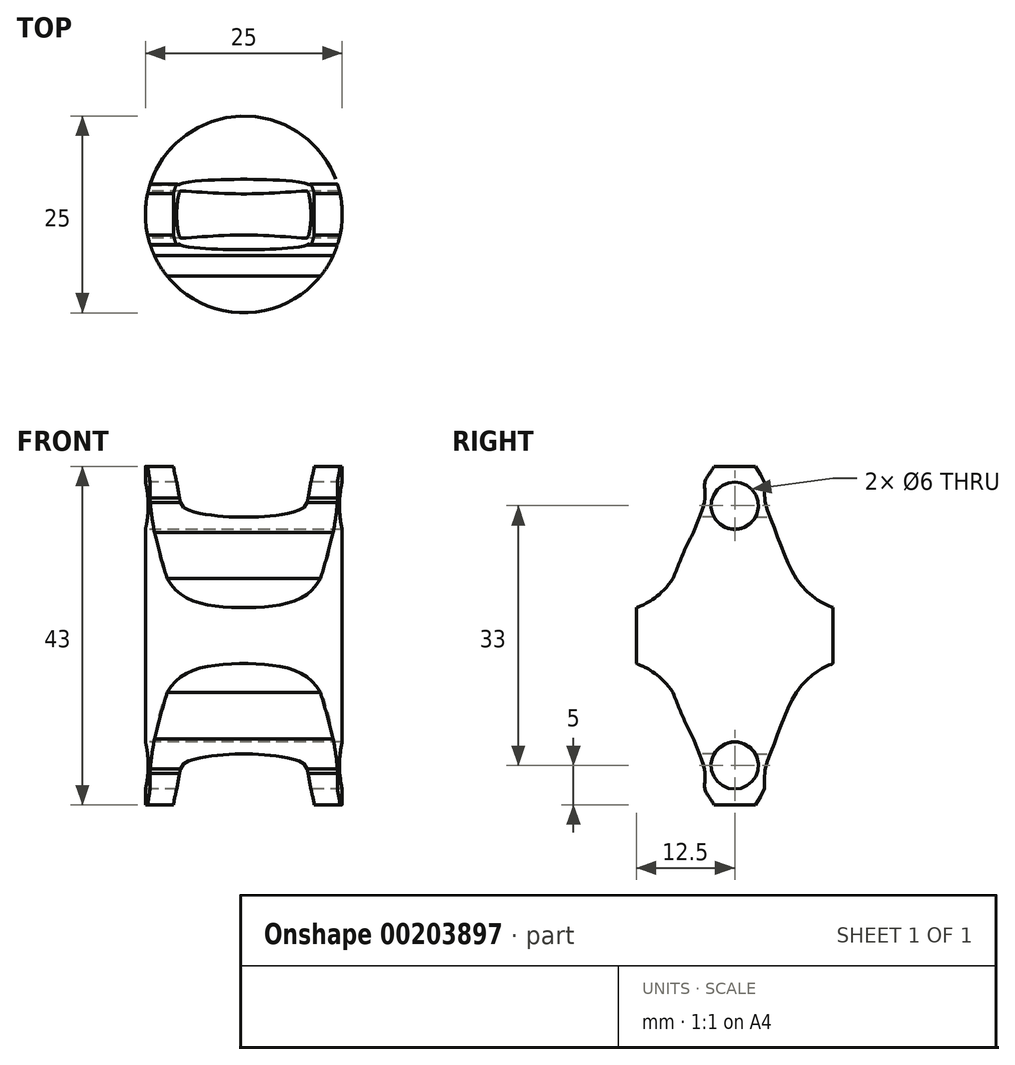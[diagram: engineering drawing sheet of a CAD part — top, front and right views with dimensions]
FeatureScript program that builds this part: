
annotation { "Feature Type Name" : "Feature", "Feature Type Description" : "" }
export const myFeature = defineFeature(function(context is Context, id is Id, definition is map)
    precondition{}
    {
        {
            var Q0;
            Q0=qCreatedBy(makeId("Top.planeOp"),FACE);
            var sketch = newSketch(context, id + "F0", { "sketchPlane" : qUnion([Q0])});
            skCircle(sketch, "E0", {"center": v(0, 0) * mm, "radius": 12.5 * mm});
            skSolve(sketch);
        }
        {
            var Q0;
            Q0=makeQuery(id+"F0.imprint","IMPRINT",FACE,{"disambiguationData":[TD([[makeQuery(id+"F0.imprint","IMPRINT",EDGE,{"derivedFrom":sQuery(id+"F0.wireOp",EDGE,"E0")}),1.0]])]});
            extrude(context, id + "F1", {"entities" : qUnion([Q0]), "depth" : 3.5 * mm});
        }
        {
            var Q0;
            Q0=makeQuery(id+"F1.opExtrude","CAP_FACE",FACE,{"disambiguationData":[OSD([sQuery(id+"F0.wireOp",EDGE,"E0")])],"isStart":false});
            extrude(context, id + "F2", {"entities" : qUnion([Q0]), "operationType" : NewBodyOperationType.ADD, "depth" : 18 * mm});
        }
        {
            var Q0;
            Q0=qCreatedBy(makeId("Right.planeOp"),FACE);
            var sketch = newSketch(context, id + "F3", { "sketchPlane" : qUnion([Q0])});
            skCircle(sketch, "E1", {"center": v(0, 16.5) * mm, "radius": 3 * mm});
            skLineSegment(sketch, "E2", {"start": v(-12.63, 3.5) * mm, "end": v(12.63, 3.5) * mm});
            skFitSpline(sketch, "E3", {"points": [v(-12.63, 3.5) * mm, v(-7.83, 7.25) * mm, v(-5.24, 13.1) * mm, v(-3.77, 17.5) * mm, v(-3.77, 19.53) * mm, v(-2.65, 21.5) * mm], "startDerivative": vector(24.86, 8.48) * mm, "endDerivative": vector(7.63, 15.3) * mm});
            skFitSpline(sketch, "E4", {"points": [v(-3.77, 17.5) * mm, v(-5.24, 13.1) * mm, v(-7.83, 7.25) * mm], "startDerivative": vector(-3.74, -25.65) * mm, "endDerivative": vector(-2.37, -6.27) * mm});
            skFitSpline(sketch, "E5.MirrorCS", {"points": [v(12.63, 3.5) * mm, v(7.83, 7.25) * mm, v(5.24, 13.1) * mm, v(3.77, 17.5) * mm, v(3.77, 19.53) * mm, v(2.65, 21.5) * mm], "startDerivative": vector(-24.86, 8.48) * mm, "endDerivative": vector(-7.63, 15.3) * mm});
            skLineSegment(sketch, "E6", {"start": v(-1.86, 21.5) * mm, "end": v(2.65, 21.5) * mm});
            skLineSegment(sketch, "E7", {"start": v(-12.5, 0) * mm, "end": v(-12.5, 31) * mm});
            skLineSegment(sketch, "E8", {"start": v(12.5, 31) * mm, "end": v(12.5, 0) * mm});
            skLineSegment(sketch, "E9", {"start": v(-12.5, 0) * mm, "end": v(12.5, 0) * mm});
            skLineSegment(sketch, "E10", {"start": v(-2.65, 21.5) * mm, "end": v(2.65, 21.5) * mm});
            skSolve(sketch);
        }
        {
            var Q0;
            Q0=qSketchRegion(id+"F3",true);
            extrude(context, id + "F4", {"entities" : qUnion([Q0]), "operationType" : NewBodyOperationType.INTERSECT, "depth" : 25 * mm, "hasSecondDirection" : true, "secondDirectionOppositeDirection" : true, "secondDirectionDepth" : 25 * mm});
        }
        {
            var Q0;
            Q0=qCreatedBy(makeId("Front.planeOp"),FACE);
            var sketch = newSketch(context, id + "F5", { "sketchPlane" : qUnion([Q0])});
            skFitSpline(sketch, "E11.0", {"points": [v(-11.71, 31) * mm, v(-11.62, 30.5) * mm, v(-11.48, 29.74) * mm, v(-11.34, 28.68) * mm, v(-11.27, 27.86) * mm, v(-11.23, 27.02) * mm, v(-11.2, 25.9) * mm, v(-11.16, 24.47) * mm, v(-11.1, 23.06) * mm, v(-11.02, 21.95) * mm, v(-10.91, 21.12) * mm, v(-10.76, 20.31) * mm, v(-10.59, 19.5) * mm, v(-10.43, 18.84) * mm, v(-10.32, 18.3) * mm, v(-10.23, 17.74) * mm, v(-10.12, 17.03) * mm, v(-9.97, 16.35) * mm, v(-9.8, 15.85) * mm, v(-9.62, 15.5) * mm, v(-9.42, 15.2) * mm, v(-9.1, 14.86) * mm, v(-8.66, 14.52) * mm, v(-8.06, 14.2) * mm, v(-7.4, 13.96) * mm, v(-6.72, 13.76) * mm, v(-6, 13.59) * mm, v(-5.23, 13.44) * mm, v(-4.44, 13.32) * mm, v(-3.63, 13.23) * mm, v(-2.8, 13.15) * mm, v(-1.95, 13.1) * mm, v(-1.1, 13.06) * mm, v(0.05, 13.04) * mm, v(1.19, 13.06) * mm, v(2.33, 13.12) * mm, v(3.45, 13.2) * mm, v(4.53, 13.33) * mm, v(5.56, 13.5) * mm, v(6.32, 13.66) * mm, v(7.03, 13.84) * mm, v(7.7, 14.06) * mm, v(8.33, 14.34) * mm, v(8.81, 14.63) * mm, v(9.16, 14.92) * mm, v(9.4, 15.17) * mm, v(9.6, 15.46) * mm, v(9.77, 15.8) * mm, v(9.9, 16.18) * mm, v(10.05, 16.7) * mm, v(10.18, 17.4) * mm, v(10.3, 18.24) * mm, v(10.48, 19.06) * mm, v(10.67, 19.86) * mm, v(10.83, 20.67) * mm, v(10.97, 21.5) * mm, v(11.06, 22.35) * mm, v(11.1, 23.23) * mm, v(11.15, 24.4) * mm, v(11.19, 25.88) * mm, v(11.24, 27.35) * mm, v(11.32, 28.5) * mm, v(11.46, 29.64) * mm, v(11.61, 30.46) * mm, v(11.71, 31) * mm]});
            skFitSpline(sketch, "E12.0", {"points": [v(-9.75, 31.36) * mm, v(-9.7, 31.11) * mm, v(-9.6, 30.6) * mm, v(-9.47, 29.78) * mm, v(-9.35, 28.9) * mm, v(-9.28, 28) * mm, v(-9.23, 27.1) * mm, v(-9.2, 25.95) * mm, v(-9.16, 24.8) * mm, v(-9.13, 23.7) * mm, v(-9.1, 23.04) * mm, v(-9.06, 22.52) * mm, v(-9.03, 22.15) * mm, v(-8.98, 21.8) * mm, v(-8.91, 21.31) * mm, v(-8.8, 20.72) * mm, v(-8.67, 20.09) * mm, v(-8.54, 19.55) * mm, v(-8.46, 19.19) * mm, v(-8.4, 18.88) * mm, v(-8.36, 18.65) * mm, v(-8.32, 18.42) * mm, v(-8.27, 18.13) * mm, v(-8.21, 17.78) * mm, v(-8.12, 17.27) * mm, v(-8.03, 16.87) * mm, v(-7.94, 16.6) * mm, v(-7.88, 16.49) * mm, v(-7.85, 16.45) * mm, v(-7.82, 16.42) * mm, v(-7.78, 16.37) * mm, v(-7.71, 16.31) * mm, v(-7.6, 16.23) * mm, v(-7.43, 16.14) * mm, v(-7.17, 16.01) * mm, v(-6.78, 15.86) * mm, v(-6.21, 15.7) * mm, v(-5.59, 15.54) * mm, v(-4.9, 15.42) * mm, v(-4.17, 15.3) * mm, v(-3.42, 15.22) * mm, v(-2.65, 15.15) * mm, v(-1.85, 15.1) * mm, v(-1.03, 15.06) * mm, v(0.05, 15.04) * mm, v(1.12, 15.06) * mm, v(2.2, 15.11) * mm, v(3.26, 15.2) * mm, v(4.26, 15.31) * mm, v(5.2, 15.47) * mm, v(5.87, 15.6) * mm, v(6.47, 15.76) * mm, v(7, 15.94) * mm, v(7.36, 16.1) * mm, v(7.57, 16.22) * mm, v(7.7, 16.3) * mm, v(7.79, 16.38) * mm, v(7.84, 16.44) * mm, v(7.87, 16.48) * mm, v(7.93, 16.6) * mm, v(8, 16.77) * mm, v(8.07, 17.04) * mm, v(8.14, 17.36) * mm, v(8.2, 17.73) * mm, v(8.26, 18.07) * mm, v(8.3, 18.37) * mm, v(8.35, 18.6) * mm, v(8.4, 18.83) * mm, v(8.45, 19.13) * mm, v(8.53, 19.5) * mm, v(8.62, 19.9) * mm, v(8.71, 20.3) * mm, v(8.8, 20.67) * mm, v(8.89, 21.16) * mm, v(8.98, 21.75) * mm, v(9.09, 22.76) * mm, v(9.15, 24.16) * mm, v(9.18, 25.63) * mm, v(9.22, 26.83) * mm, v(9.26, 27.6) * mm, v(9.3, 28.22) * mm, v(9.35, 28.85) * mm, v(9.45, 29.64) * mm, v(9.6, 30.54) * mm, v(9.7, 31.1) * mm, v(9.75, 31.36) * mm]});
            skLineSegment(sketch, "E13", {"start": v(12.22, 21.5) * mm, "end": v(10.23, 21.71) * mm});
            skLineSegment(sketch, "E14", {"start": v(-12.22, 21.5) * mm, "end": v(-10.23, 21.71) * mm});
            skLineSegment(sketch, "E15", {"start": v(10.23, 21.71) * mm, "end": v(-10.23, 21.71) * mm});
            skSolve(sketch);
        }
        {
            var Q0;
            Q0=makeQuery(id+"F5.imprint","IMPRINT",FACE,{"disambiguationData":[TD([[makeQuery(id+"F5.imprint","IMPRINT",EDGE,{"derivedFrom":sQuery(id+"F5.wireOp",EDGE,"E12.0")}),1.0]])]});
            extrude(context, id + "F6", {"entities" : qUnion([Q0]), "operationType" : NewBodyOperationType.REMOVE, "depth" : 25 * mm, "hasSecondDirection" : true, "secondDirectionOppositeDirection" : true, "secondDirectionDepth" : 25 * mm});
        }
        {
            var Q0;
            Q0=makeQuery(id+"F1.opExtrude","SWEPT_BODY",BODY,{"disambiguationData":[OSD([sQuery(id+"F0.wireOp",EDGE,"E0")])]});
            var Q1;
            Q1=qCreatedBy(makeId("Top.planeOp"),FACE);
            mirror(context, id + "F7", {"operationType" : NewBodyOperationType.ADD, "entities" : qUnion([Q0]), "mirrorPlane" : qUnion([Q1])});
        }
    });
